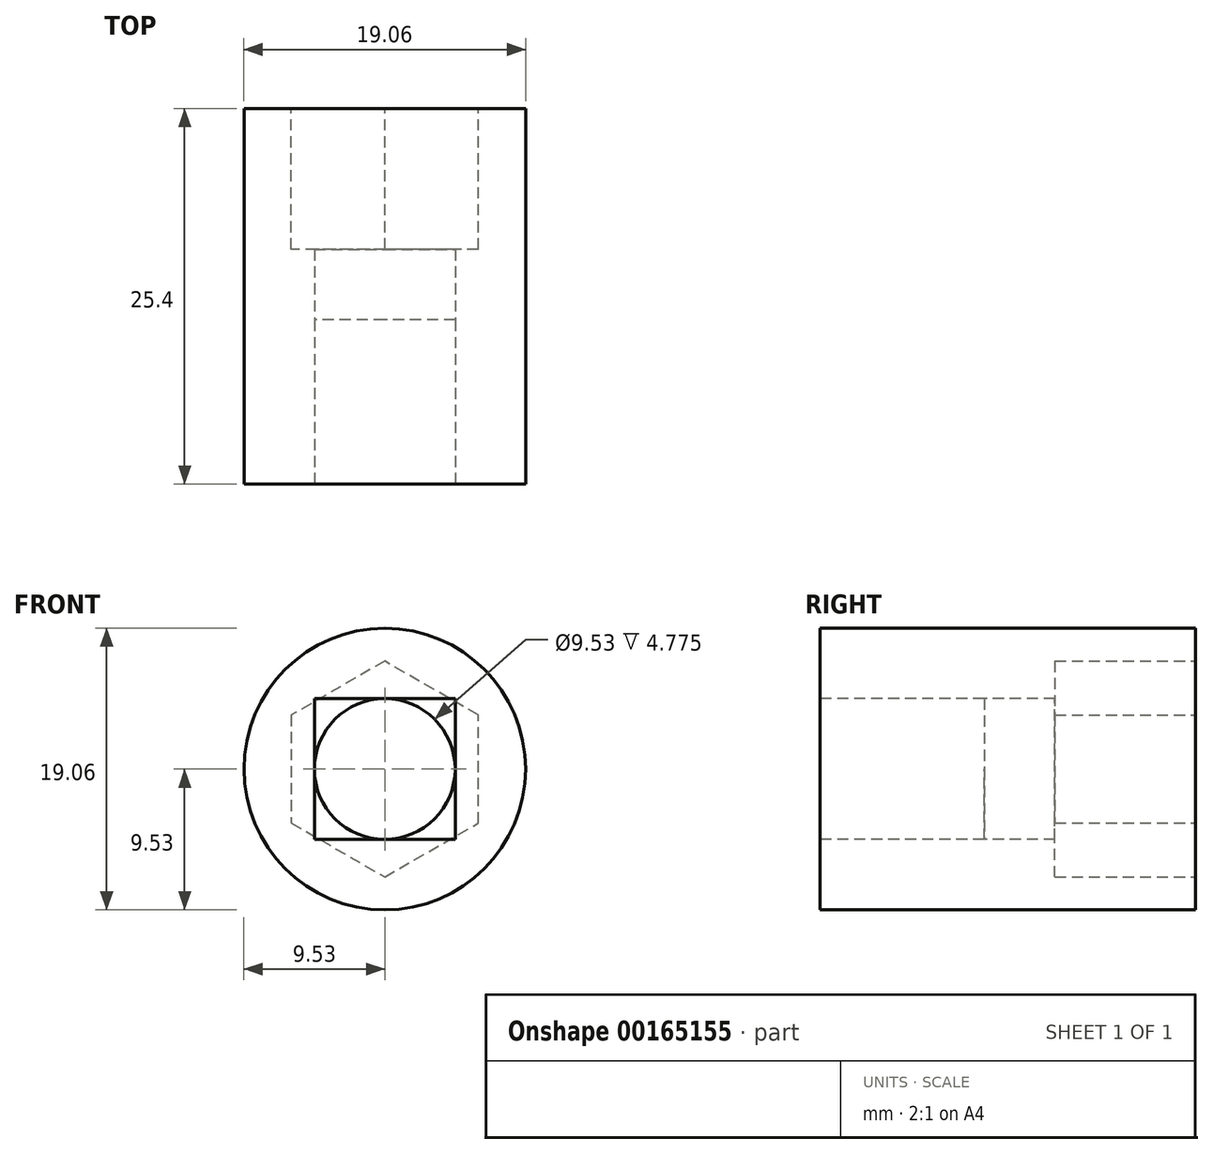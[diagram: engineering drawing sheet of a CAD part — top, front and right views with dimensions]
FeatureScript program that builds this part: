
annotation { "Feature Type Name" : "Feature", "Feature Type Description" : "" }
export const myFeature = defineFeature(function(context is Context, id is Id, definition is map)
    precondition{}
    {
        {
            var Q0;
            Q0=qCreatedBy(makeId("Front.planeOp"),FACE);
            var sketch = newSketch(context, id + "F0", { "sketchPlane" : qUnion([Q0])});
            skCircle(sketch, "E0", {"center": v(0, 0) * mm, "radius": 9.53 * mm});
            skSolve(sketch);
        }
        {
            var Q0;
            Q0 = qSketchRegion(id + "F0", true);
            extrude(context, id + "F1", {"entities" : qUnion([Q0]), "depth" : 25.4 * mm});
        }
        {
            var Q0;
            Q0=makeQuery(id+"F1.opExtrude","CAP_FACE",FACE,{"disambiguationData":[OSD([sQuery(id+"F0.wireOp",EDGE,"E0")])],"isStart":false});
            var sketch = newSketch(context, id + "F2", { "sketchPlane" : qUnion([Q0])});
            skLineSegment(sketch, "E1.bottom", {"start": v(4.76, 4.76) * mm, "end": v(-4.76, 4.76) * mm});
            skLineSegment(sketch, "E1.top", {"start": v(4.76, -4.76) * mm, "end": v(-4.76, -4.76) * mm});
            skLineSegment(sketch, "E1.left", {"start": v(4.76, 4.76) * mm, "end": v(4.76, -4.76) * mm});
            skLineSegment(sketch, "E1.right", {"start": v(-4.76, 4.76) * mm, "end": v(-4.76, -4.76) * mm});
            skPoint(sketch, "E1.middle", {"position": v(0, 0) * mm});
            skCircle(sketch, "E2", {"center": v(0, 0) * mm, "radius": 4.76 * mm});
            skSolve(sketch);
        }
        {
            var Q0;
            {var subQ0=sQuery(id+"F2.wireOp",EDGE,"E2");var subQ1=makeQuery(id+"F2.imprint","INTERSECT",VERTEX,{"derivedFrom":[sQuery(id+"F2.wireOp",EDGE,"E1.bottom"),subQ0]});Q0=makeQuery(id+"F2.imprint","IMPRINT",FACE,{"disambiguationData":[TD([[makeQuery(id+"F2.imprint","IMPRINT",EDGE,{"disambiguationData":[TD([[subQ1,1.0]])],"derivedFrom":subQ0}),1.0]])]});}
            extrude(context, id + "F3", {"entities" : qUnion([Q0]), "operationType" : NewBodyOperationType.REMOVE, "endBound" : BoundingType.THROUGH_ALL, "oppositeDirection" : true, "depth" : 25.4 * mm});
        }
        {
            var Q0;
            Q0 = qSketchRegion(id + "F2", true);
            extrude(context, id + "F4", {"entities" : qUnion([Q0]), "operationType" : NewBodyOperationType.REMOVE, "oppositeDirection" : true, "depth" : 11.1 * mm});
        }
        {
            var Q0;
            Q0=makeQuery(id+"F1.opExtrude","CAP_FACE",FACE,{"disambiguationData":[OSD([sQuery(id+"F0.wireOp",EDGE,"E0")])],"isStart":true});
            var sketch = newSketch(context, id + "F5", { "sketchPlane" : qUnion([Q0])});
            skCircle(sketch, "E3.cCircle", {"center": v(0, 0) * mm, "radius": 6.32 * mm, "construction": true});
            skLineSegment(sketch, "E3.0", {"start": v(6.32, 3.65) * mm, "end": v(6.32, -3.65) * mm});
            skLineSegment(sketch, "E3.1", {"start": v(6.32, -3.65) * mm, "end": v(0, -7.3) * mm});
            skLineSegment(sketch, "E3.2", {"start": v(0, -7.3) * mm, "end": v(-6.32, -3.65) * mm});
            skLineSegment(sketch, "E3.3", {"start": v(-6.32, -3.65) * mm, "end": v(-6.32, 3.65) * mm});
            skLineSegment(sketch, "E3.4", {"start": v(-6.32, 3.65) * mm, "end": v(0, 7.3) * mm});
            skLineSegment(sketch, "E3.5", {"start": v(0, 7.3) * mm, "end": v(6.32, 3.65) * mm});
            skPoint(sketch, "E3.0.midPoint", {"position": v(6.32, 0) * mm});
            skSolve(sketch);
        }
        {
            var Q0;
            Q0=makeQuery(id+"F5.imprint","IMPRINT",FACE,{"disambiguationData":[TD([[makeQuery(id+"F5.imprint","IMPRINT",EDGE,{"derivedFrom":sQuery(id+"F5.wireOp",EDGE,"E3.0")}),-1.0]])]});
            extrude(context, id + "F6", {"entities" : qUnion([Q0]), "operationType" : NewBodyOperationType.REMOVE, "oppositeDirection" : true, "depth" : 9.52 * mm});
        }
    });
